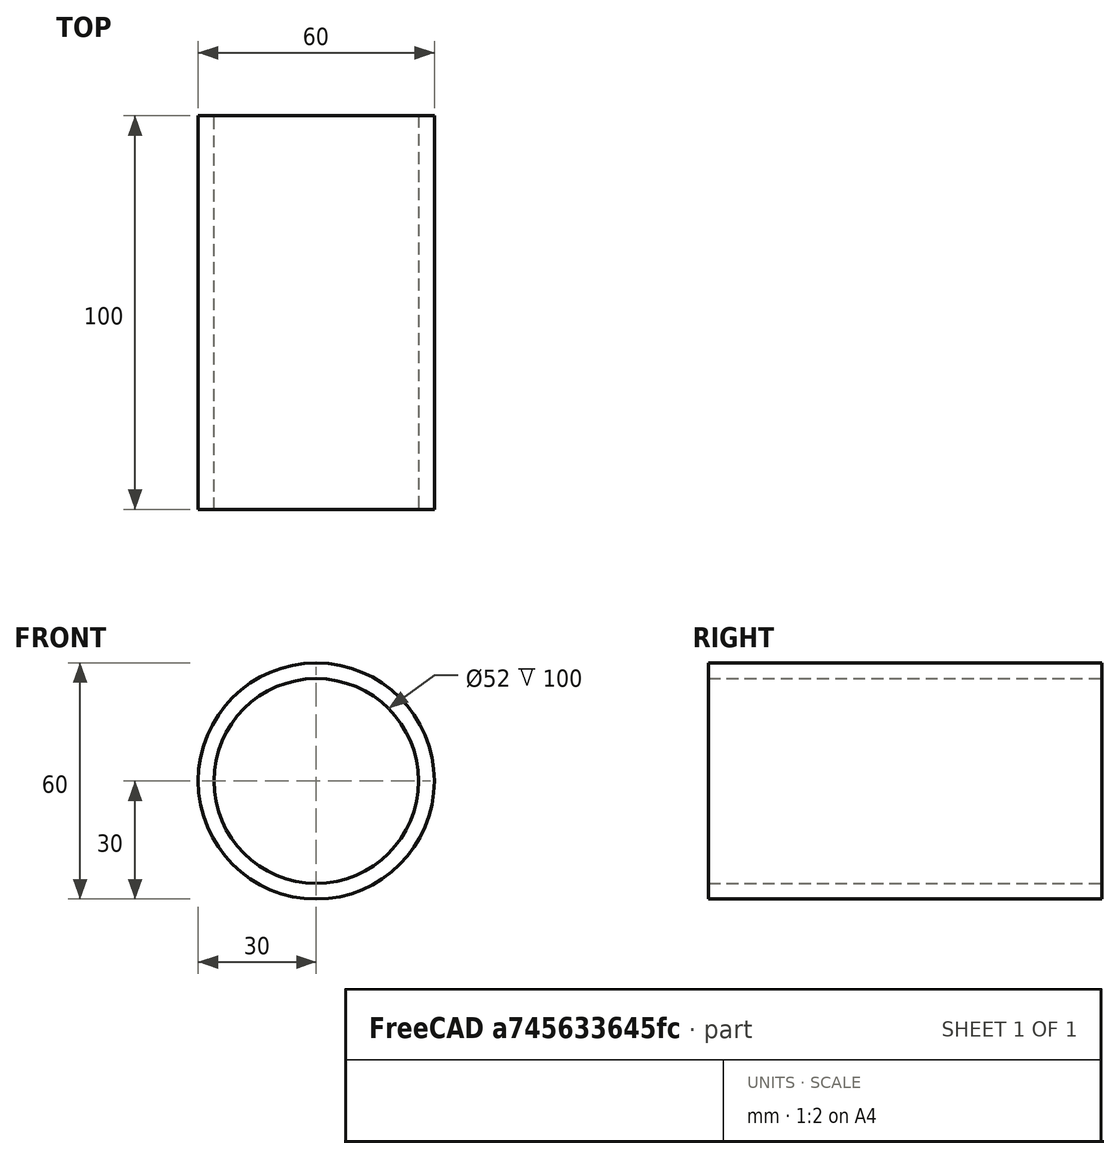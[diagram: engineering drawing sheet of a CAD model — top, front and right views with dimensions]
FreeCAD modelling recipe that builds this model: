
FCSTD DOCUMENT  (FreeCAD 0.21R33771 (Git))
Label: Acrylrohr 60mm
License: All rights reserved
LicenseURL: http://en.wikipedia.org/wiki/All_rights_reserved
objects: Sketcher::SketchObject×1, PartDesign::Pad×1, PartDesign::Body×1
note: 4 computed .brp shape members not serialized (recipe doc carries the construction recipe); baked Part::Feature solids carry a one-line shape summary decoded from their .brp

FEATURE [Sketcher::SketchObject] Sketch
  FullyConstrained = true
  MapMode = 5
  Placement = pos=(0,0,0) rot=(1,0,0;1.5708rad)
  Support = -> [XZ_Plane]
  sketch-geometry (2):
    g0: Circle CenterX=0 CenterY=0 CenterZ=0 NormalX=0 NormalY=0 NormalZ=1 AngleXU=0 Radius=30
    g1: Circle CenterX=0 CenterY=0 CenterZ=0 NormalX=0 NormalY=0 NormalZ=1 AngleXU=0 Radius=27
  constraints (4):
    c: Coincident(g0,g-1)
    c: Radius(g0) = 30
    c: Coincident(g1,g0)
    c: Radius(g1) = 27
FEATURE [PartDesign::Pad] Pad
  Direction = (1,1,1)
  Length = 100
  Length2 = 100
  Placement = pos=(0,0,0) rot=(1,0,0;1.5708rad)
  Profile = -> Sketch
  Type = 0
FEATURE [PartDesign::Body] Body
  Group = -> [Sketch,Pad]
  Origin = -> Origin
  Tip = -> Pad
